# Revit family: Domotics-DomesticRanges-GEWISS-SYSTEM_PLATES_SUPPORT_DOUBLE
name_source: partatom
category: Apparecchi elettrici
revit_build: Autodesk Revit 2016 (Build: 20161004_0715(x64)
units: mm (PartAtom-declared; Revit-internal decimal feet)

## family parameters
Basato su piano di lavoro = Sì
Condiviso = Sì
Mantenere orientamento annotazione = Sì
Punto di calcolo locali = Sì
Quota connettore circolare = Usa diametro
Sempre verticale = Sì
Taglio con vuoti quando caricato = No
Tipo di parte = Normale

## types (2) — shared parameters
Altezza foro = 45 mm  [stored 0.147638 ft]
Altezza supporto = 135 mm  [stored 0.442913 ft]
Catalogue = BUILDING
Catalogue Range = 40 CDE
Characteristics = Halogen free
Configuration = Overlapping
Electrocod = 0121
Fixing = 4 screws (included)
IDF = 0c3e690f-6b00-47a6-823b-121b99ea53ec
IDT = 9cd5ad26-df35-4942-9ec7-442b70415c37
Immagine tipo = <Nessuno>
Larghezza foro = 138 mm  [stored 0.452756 ft]
Larghezza supporto = 184 mm  [stored 0.603675 ft]
Materiale supporto = GEWISS - ACCIAIO SUPPORTO
Produttore = GEWISS S.p.A.
Prospetto di default = 1219.2 mm  [stored 4 ft]
SEO = Support
Technical sheet = https://www.gewiss.com
URL = https://www.gewiss.com
Version file RFA = 19.4

## per-type parameters (varying)
| type | Description: | Descrizione | EAN code | Modello |
| GW24240 - 8 GANG SUPPORT FOR SYSTEM-VIRNA PLATE | 4+4 gang | 8 GANG SUPPORT FOR SYSTEM/VIRNA PLATE | 8011564130111 | GW24240 |
| GW24241 - 12 GANG SUPPORT FOR SYSTEM-VIRNA PLATE | 6+6 gang | 12 GANG SUPPORT FOR SYSTEM/VIRNA PLATE | 8011564130128 | GW24241 |

note: [stored X ft] marks values corroborated as IEEE doubles in the binary element streams (Revit-internal decimal feet)
